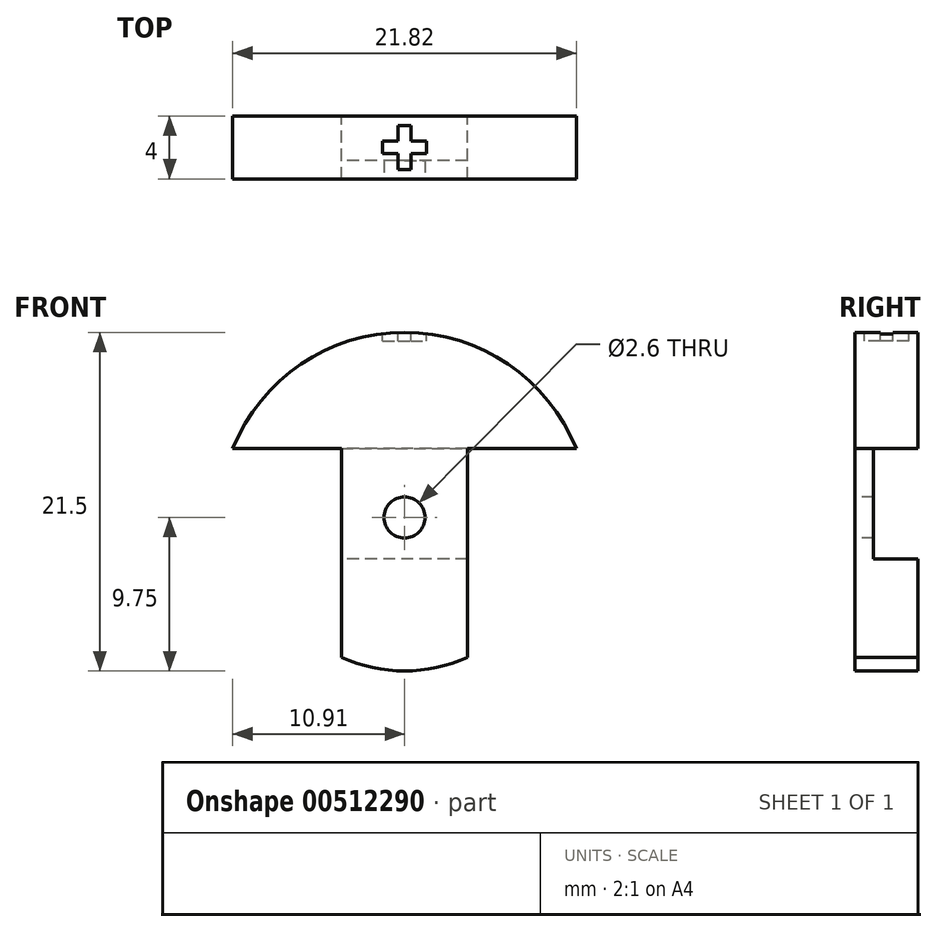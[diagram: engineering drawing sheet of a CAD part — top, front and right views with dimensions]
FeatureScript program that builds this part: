
annotation { "Feature Type Name" : "Feature", "Feature Type Description" : "" }
export const myFeature = defineFeature(function(context is Context, id is Id, definition is map)
    precondition{}
    {
        {
            var Q0;
            Q0=qCreatedBy(makeId("Front.planeOp"),FACE);
            var sketch = newSketch(context, id + "F0", { "sketchPlane" : qUnion([Q0])});
            skArc(sketch, "E0", {"start": v(-4, -8.9) * mm, "mid": v(0, -9.75) * mm, "end": v(4, -8.9) * mm});
            skLineSegment(sketch, "E1", {"start": v(-10.9, 4.37) * mm, "end": v(-4, 4.37) * mm});
            skArc(sketch, "E2", {"start": v(10.9, 4.37) * mm, "mid": v(0, 11.75) * mm, "end": v(-10.9, 4.37) * mm});
            skLineSegment(sketch, "E3.trimOffspring", {"start": v(4, 4.37) * mm, "end": v(10.9, 4.37) * mm});
            skLineSegment(sketch, "E4", {"start": v(0, -9.75) * mm, "end": v(0, 11.75) * mm, "construction": true});
            skLineSegment(sketch, "E5", {"start": v(-4, -8.9) * mm, "end": v(-4, 4.37) * mm});
            skLineSegment(sketch, "E6", {"start": v(4, -8.9) * mm, "end": v(4, 4.37) * mm});
            skPoint(sketch, "E7.orphan", {"position": v(4, 2.99) * mm});
            skPoint(sketch, "E8.orphan", {"position": v(-4, 2.99) * mm});
            skSolve(sketch);
        }
        {
            var Q0;
            Q0 = qSketchRegion(id + "F0", true);
            extrude(context, id + "F1", {"entities" : qUnion([Q0]), "depth" : 4 * mm, "offsetDistance" : 25 * mm});
        }
        {
            var Q0;
            Q0=qCreatedBy(makeId("Right.planeOp"),FACE);
            var sketch = newSketch(context, id + "F2", { "sketchPlane" : qUnion([Q0])});
            skLineSegment(sketch, "E9.0", {"start": v(-2.83, 4.37) * mm, "end": v(0, 4.37) * mm});
            skLineSegment(sketch, "E10.0", {"start": v(0, -2.63) * mm, "end": v(0, 4.37) * mm});
            skLineSegment(sketch, "E11", {"start": v(-2.83, 4.37) * mm, "end": v(-2.83, -2.63) * mm});
            skLineSegment(sketch, "E12", {"start": v(-2.83, -2.63) * mm, "end": v(0, -2.63) * mm});
            skPoint(sketch, "E13.orphan", {"position": v(-4, 4.37) * mm});
            skPoint(sketch, "E14.orphan", {"position": v(0, -8.9) * mm});
            skSolve(sketch);
        }
        {
            var Q0;
            Q0 = qSketchRegion(id + "F2", true);
            extrude(context, id + "F3", {"entities" : qUnion([Q0]), "operationType" : NewBodyOperationType.REMOVE, "endBound" : BoundingType.SYMMETRIC, "depth" : 25 * mm, "offsetDistance" : 25 * mm});
        }
        {
            var Q0;
            Q0=qCreatedBy(makeId("Top.planeOp"),FACE);
            cPlane(context, id + "F4", {"entities" : qUnion([Q0]), "cplaneType" : CPlaneType.OFFSET, "offset" : 12 * mm, "width" : 150 * mm, "height" : 150 * mm});
        }
        {
            var Q0;
            Q0=qCreatedBy(id+"F4.planeOp",FACE);
            var sketch = newSketch(context, id + "F5", { "sketchPlane" : qUnion([Q0])});
            skLineSegment(sketch, "E15", {"start": v(0, 0) * mm, "end": v(0, -5.95) * mm, "construction": true});
            skLineSegment(sketch, "E16", {"start": v(-4.38, -2) * mm, "end": v(4.62, -2) * mm, "construction": true});
            skLineSegment(sketch, "E17.bottom", {"start": v(-1.4, -1.6) * mm, "end": v(-0.4, -1.6) * mm});
            skLineSegment(sketch, "E17.top", {"start": v(-1.4, -2.4) * mm, "end": v(-0.4, -2.4) * mm});
            skLineSegment(sketch, "E17.left", {"start": v(-1.4, -1.6) * mm, "end": v(-1.4, -2.4) * mm});
            skLineSegment(sketch, "E17.right", {"start": v(1.4, -1.6) * mm, "end": v(1.4, -2.4) * mm});
            skLineSegment(sketch, "E18.bottom", {"start": v(-0.4, -0.6) * mm, "end": v(0.4, -0.6) * mm});
            skLineSegment(sketch, "E18.top", {"start": v(-0.4, -3.4) * mm, "end": v(0.4, -3.4) * mm});
            skLineSegment(sketch, "E18.left", {"start": v(-0.4, -0.6) * mm, "end": v(-0.4, -1.6) * mm});
            skLineSegment(sketch, "E18.right", {"start": v(0.4, -0.6) * mm, "end": v(0.4, -1.6) * mm});
            skLineSegment(sketch, "E19.trimOffspring", {"start": v(0.4, -1.6) * mm, "end": v(1.4, -1.6) * mm});
            skLineSegment(sketch, "E20.trimOffspring", {"start": v(-0.4, -2.4) * mm, "end": v(-0.4, -3.4) * mm});
            skLineSegment(sketch, "E21.trimOffspring", {"start": v(0.4, -2.4) * mm, "end": v(1.4, -2.4) * mm});
            skLineSegment(sketch, "E22.trimOffspring", {"start": v(0.4, -2.4) * mm, "end": v(0.4, -3.4) * mm});
            skSolve(sketch);
        }
        {
            var Q0;
            Q0 = qSketchRegion(id + "F5", true);
            extrude(context, id + "F6", {"entities" : qUnion([Q0]), "operationType" : NewBodyOperationType.REMOVE, "oppositeDirection" : true, "depth" : .8 * mm, "offsetDistance" : 25 * mm});
        }
        {
            var Q0;
            Q0=makeQuery(id+"F1.opExtrude","CAP_FACE",FACE,{"disambiguationData":[OSD([sQuery(id+"F0.wireOp",EDGE,"E0"),sQuery(id+"F0.wireOp",EDGE,"E1"),sQuery(id+"F0.wireOp",EDGE,"E2"),sQuery(id+"F0.wireOp",EDGE,"E3.trimOffspring"),sQuery(id+"F0.wireOp",EDGE,"E5"),sQuery(id+"F0.wireOp",EDGE,"E6")])],"isStart":false});
            var sketch = newSketch(context, id + "F7", { "sketchPlane" : qUnion([Q0])});
            skCircle(sketch, "E23", {"center": v(0, 0) * mm, "radius": 1.3 * mm});
            skSolve(sketch);
        }
        {
            var Q0;
            Q0 = qSketchRegion(id + "F7", true);
            extrude(context, id + "F8", {"entities" : qUnion([Q0]), "operationType" : NewBodyOperationType.REMOVE, "endBound" : BoundingType.THROUGH_ALL, "oppositeDirection" : true, "depth" : .4 * mm, "offsetDistance" : 25 * mm});
        }
    });
